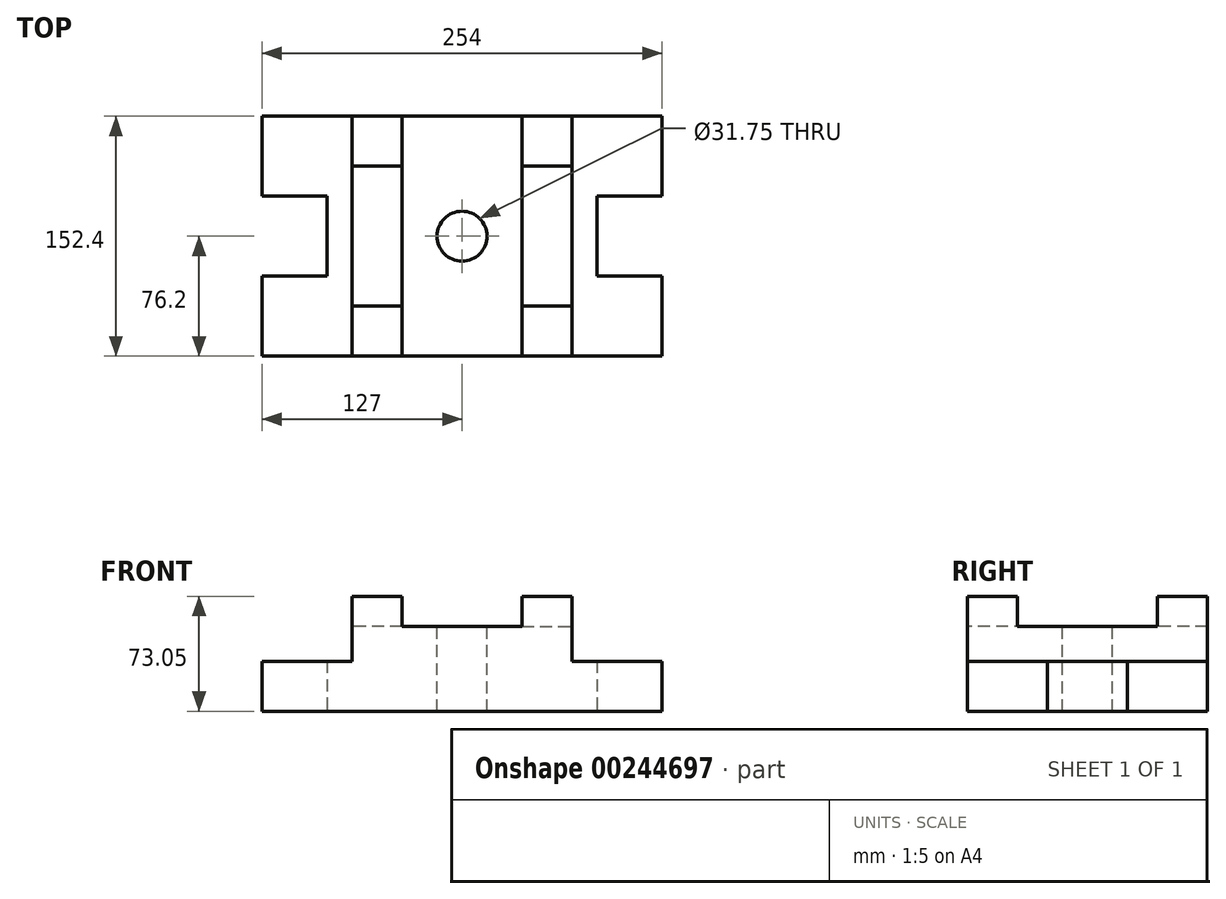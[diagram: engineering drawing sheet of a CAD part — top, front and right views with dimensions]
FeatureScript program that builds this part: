
annotation { "Feature Type Name" : "Feature", "Feature Type Description" : "" }
export const myFeature = defineFeature(function(context is Context, id is Id, definition is map)
    precondition{}
    {
        {
            var Q0;
            Q0=qCreatedBy(makeId("Top.planeOp"),FACE);
            var sketch = newSketch(context, id + "F0", { "sketchPlane" : qUnion([Q0])});
            skLineSegment(sketch, "E0.bottom", {"start": v(127, 76.2) * mm, "end": v(-127, 76.2) * mm});
            skLineSegment(sketch, "E0.top", {"start": v(127, -76.2) * mm, "end": v(-127, -76.2) * mm});
            skPoint(sketch, "E0.middle", {"position": v(0, 0) * mm});
            skLineSegment(sketch, "E1", {"start": v(-127, -76.2) * mm, "end": v(-127, -25.4) * mm});
            skLineSegment(sketch, "E2.bottom", {"start": v(-127, -25.4) * mm, "end": v(-85.72, -25.4) * mm});
            skLineSegment(sketch, "E2.top", {"start": v(-127, 25.4) * mm, "end": v(-85.72, 25.4) * mm});
            skLineSegment(sketch, "E2.right", {"start": v(-85.72, -25.4) * mm, "end": v(-85.72, 25.4) * mm});
            skLineSegment(sketch, "E3", {"start": v(-127, 25.4) * mm, "end": v(-127, 76.2) * mm});
            skLineSegment(sketch, "E4", {"start": v(127, -76.2) * mm, "end": v(127, -25.4) * mm});
            skLineSegment(sketch, "E5.bottom", {"start": v(127, -25.4) * mm, "end": v(85.73, -25.4) * mm});
            skLineSegment(sketch, "E5.top", {"start": v(127, 25.4) * mm, "end": v(85.73, 25.4) * mm});
            skLineSegment(sketch, "E5.right", {"start": v(85.73, -25.4) * mm, "end": v(85.73, 25.4) * mm});
            skLineSegment(sketch, "E6", {"start": v(127, 76.2) * mm, "end": v(127, 25.4) * mm});
            skSolve(sketch);
        }
        {
            var Q0;
            Q0=makeQuery(id+"F0.imprint","IMPRINT",FACE,{"disambiguationData":[TD([[makeQuery(id+"F0.imprint","IMPRINT",EDGE,{"derivedFrom":sQuery(id+"F0.wireOp",EDGE,"E0.bottom")}),1.0]])]});
            extrude(context, id + "F1", {"entities" : qUnion([Q0]), "depth" : 31.75 * mm});
        }
        {
            var Q0;
            Q0=makeQuery(id+"F1.opExtrude","CAP_FACE",FACE,{"disambiguationData":[OSD([sQuery(id+"F0.wireOp",EDGE,"E0.bottom"),sQuery(id+"F0.wireOp",EDGE,"E0.top"),sQuery(id+"F0.wireOp",EDGE,"E1"),sQuery(id+"F0.wireOp",EDGE,"E2.bottom"),sQuery(id+"F0.wireOp",EDGE,"E2.top"),sQuery(id+"F0.wireOp",EDGE,"E2.right"),sQuery(id+"F0.wireOp",EDGE,"E3"),sQuery(id+"F0.wireOp",EDGE,"E4"),sQuery(id+"F0.wireOp",EDGE,"E5.bottom"),sQuery(id+"F0.wireOp",EDGE,"E5.top"),sQuery(id+"F0.wireOp",EDGE,"E5.right"),sQuery(id+"F0.wireOp",EDGE,"E6")])],"isStart":false});
            var sketch = newSketch(context, id + "F2", { "sketchPlane" : qUnion([Q0])});
            skLineSegment(sketch, "E7.bottom", {"start": v(69.85, 76.2) * mm, "end": v(-69.85, 76.2) * mm});
            skLineSegment(sketch, "E7.top", {"start": v(69.85, -76.2) * mm, "end": v(-69.85, -76.2) * mm});
            skLineSegment(sketch, "E7.left", {"start": v(69.85, 76.2) * mm, "end": v(69.85, -76.2) * mm});
            skLineSegment(sketch, "E7.right", {"start": v(-69.85, 76.2) * mm, "end": v(-69.85, -76.2) * mm});
            skPoint(sketch, "E7.middle", {"position": v(0, 0) * mm});
            skSolve(sketch);
        }
        {
            var Q0;
            Q0=makeQuery(id+"F2.imprint","IMPRINT",FACE,{"disambiguationData":[TD([[makeQuery(id+"F2.imprint","IMPRINT",EDGE,{"derivedFrom":sQuery(id+"F2.wireOp",EDGE,"E7.bottom")}),1.0]])]});
            extrude(context, id + "F3", {"entities" : qUnion([Q0]), "operationType" : NewBodyOperationType.ADD, "depth" : 22.22 * mm});
        }
        {
            var Q0;
            Q0=makeQuery(id+"F3.opExtrude","CAP_FACE",FACE,{"disambiguationData":[OSD([sQuery(id+"F2.wireOp",EDGE,"E7.bottom"),sQuery(id+"F2.wireOp",EDGE,"E7.top"),sQuery(id+"F2.wireOp",EDGE,"E7.left"),sQuery(id+"F2.wireOp",EDGE,"E7.right")])],"isStart":false});
            var sketch = newSketch(context, id + "F4", { "sketchPlane" : qUnion([Q0])});
            skCircle(sketch, "E8", {"center": v(0, 0) * mm, "radius": 15.88 * mm});
            skSolve(sketch);
        }
        {
            var Q0;
            Q0=makeQuery(id+"F4.imprint","IMPRINT",FACE,{"disambiguationData":[TD([[makeQuery(id+"F4.imprint","IMPRINT",EDGE,{"derivedFrom":sQuery(id+"F4.wireOp",EDGE,"E8")}),1.0]])]});
            extrude(context, id + "F5", {"entities" : qUnion([Q0]), "operationType" : NewBodyOperationType.REMOVE, "endBound" : BoundingType.THROUGH_ALL, "oppositeDirection" : true, "depth" : 25.4 * mm});
        }
        {
            var Q0;
            Q0=makeQuery(id+"F3.opExtrude","CAP_FACE",FACE,{"disambiguationData":[OSD([sQuery(id+"F2.wireOp",EDGE,"E7.bottom"),sQuery(id+"F2.wireOp",EDGE,"E7.top"),sQuery(id+"F2.wireOp",EDGE,"E7.left"),sQuery(id+"F2.wireOp",EDGE,"E7.right")])],"isStart":false});
            var sketch = newSketch(context, id + "F6", { "sketchPlane" : qUnion([Q0])});
            skLineSegment(sketch, "E9.bottom", {"start": v(-69.85, 76.2) * mm, "end": v(-38.1, 76.2) * mm});
            skLineSegment(sketch, "E9.top", {"start": v(-69.85, -76.2) * mm, "end": v(-38.1, -76.2) * mm});
            skLineSegment(sketch, "E9.left", {"start": v(-69.85, 76.2) * mm, "end": v(-69.85, -76.2) * mm});
            skLineSegment(sketch, "E9.right", {"start": v(-38.1, 76.2) * mm, "end": v(-38.1, -76.2) * mm});
            skLineSegment(sketch, "E10.bottom", {"start": v(69.85, 76.2) * mm, "end": v(38.1, 76.2) * mm});
            skLineSegment(sketch, "E10.top", {"start": v(69.85, -76.2) * mm, "end": v(38.1, -76.2) * mm});
            skLineSegment(sketch, "E10.left", {"start": v(69.85, 76.2) * mm, "end": v(69.85, -76.2) * mm});
            skLineSegment(sketch, "E10.right", {"start": v(38.1, 76.2) * mm, "end": v(38.1, -76.2) * mm});
            skSolve(sketch);
        }
        {
            var Q0;
            Q0=makeQuery(id+"F6.imprint","IMPRINT",FACE,{"disambiguationData":[TD([[makeQuery(id+"F6.imprint","IMPRINT",EDGE,{"derivedFrom":sQuery(id+"F6.wireOp",EDGE,"E10.bottom")}),1.0]])]});
            var Q1;
            Q1=makeQuery(id+"F6.imprint","IMPRINT",FACE,{"disambiguationData":[TD([[makeQuery(id+"F6.imprint","IMPRINT",EDGE,{"derivedFrom":sQuery(id+"F6.wireOp",EDGE,"E9.bottom")}),1.0]])]});
            extrude(context, id + "F7", {"entities" : qUnion([Q0, Q1]), "operationType" : NewBodyOperationType.ADD, "depth" : 3 / 101.6 * mm});
        }
        {
            var Q0;
            Q0=makeQuery(id+"F7.opExtrude","CAP_FACE",FACE,{"disambiguationData":[OSD([sQuery(id+"F6.wireOp",EDGE,"E10.bottom"),sQuery(id+"F6.wireOp",EDGE,"E10.top"),sQuery(id+"F6.wireOp",EDGE,"E10.left"),sQuery(id+"F6.wireOp",EDGE,"E10.right")])],"isStart":false});
            var sketch = newSketch(context, id + "F8", { "sketchPlane" : qUnion([Q0])});
            skLineSegment(sketch, "E11.bottom", {"start": v(38.1, 76.2) * mm, "end": v(69.85, 76.2) * mm});
            skLineSegment(sketch, "E11.top", {"start": v(38.1, 44.45) * mm, "end": v(69.85, 44.45) * mm});
            skLineSegment(sketch, "E11.left", {"start": v(38.1, 76.2) * mm, "end": v(38.1, 44.45) * mm});
            skLineSegment(sketch, "E11.right", {"start": v(69.85, 76.2) * mm, "end": v(69.85, 44.45) * mm});
            skLineSegment(sketch, "E12.bottom", {"start": v(38.1, -44.45) * mm, "end": v(69.85, -44.45) * mm});
            skLineSegment(sketch, "E12.top", {"start": v(38.1, -76.2) * mm, "end": v(69.85, -76.2) * mm});
            skLineSegment(sketch, "E12.left", {"start": v(38.1, -44.45) * mm, "end": v(38.1, -76.2) * mm});
            skLineSegment(sketch, "E12.right", {"start": v(69.85, -44.45) * mm, "end": v(69.85, -76.2) * mm});
            skSolve(sketch);
        }
        {
            var Q0;
            Q0=makeQuery(id+"F7.opExtrude","CAP_FACE",FACE,{"disambiguationData":[OSD([sQuery(id+"F6.wireOp",EDGE,"E9.bottom"),sQuery(id+"F6.wireOp",EDGE,"E9.top"),sQuery(id+"F6.wireOp",EDGE,"E9.left"),sQuery(id+"F6.wireOp",EDGE,"E9.right")])],"isStart":false});
            var sketch = newSketch(context, id + "F9", { "sketchPlane" : qUnion([Q0])});
            skLineSegment(sketch, "E13.bottom", {"start": v(-69.85, -76.2) * mm, "end": v(-38.1, -76.2) * mm});
            skLineSegment(sketch, "E13.top", {"start": v(-69.85, -44.45) * mm, "end": v(-38.1, -44.45) * mm});
            skLineSegment(sketch, "E13.left", {"start": v(-69.85, -76.2) * mm, "end": v(-69.85, -44.45) * mm});
            skLineSegment(sketch, "E13.right", {"start": v(-38.1, -76.2) * mm, "end": v(-38.1, -44.45) * mm});
            skLineSegment(sketch, "E14.bottom", {"start": v(-38.1, 76.2) * mm, "end": v(-69.85, 76.2) * mm});
            skLineSegment(sketch, "E14.top", {"start": v(-38.1, 44.45) * mm, "end": v(-69.85, 44.45) * mm});
            skLineSegment(sketch, "E14.left", {"start": v(-38.1, 76.2) * mm, "end": v(-38.1, 44.45) * mm});
            skLineSegment(sketch, "E14.right", {"start": v(-69.85, 76.2) * mm, "end": v(-69.85, 44.45) * mm});
            skSolve(sketch);
        }
        {
            var Q0;
            Q0=makeQuery(id+"F9.imprint","IMPRINT",FACE,{"disambiguationData":[TD([[makeQuery(id+"F9.imprint","IMPRINT",EDGE,{"derivedFrom":sQuery(id+"F9.wireOp",EDGE,"E13.bottom")}),-1.0]])]});
            var Q1;
            Q1=makeQuery(id+"F9.imprint","IMPRINT",FACE,{"disambiguationData":[TD([[makeQuery(id+"F9.imprint","IMPRINT",EDGE,{"derivedFrom":sQuery(id+"F9.wireOp",EDGE,"E14.bottom")}),1.0]])]});
            var Q2;
            Q2=makeQuery(id+"F8.imprint","IMPRINT",FACE,{"disambiguationData":[TD([[makeQuery(id+"F8.imprint","IMPRINT",EDGE,{"derivedFrom":sQuery(id+"F8.wireOp",EDGE,"E11.bottom")}),1.0]])]});
            var Q3;
            Q3=makeQuery(id+"F8.imprint","IMPRINT",FACE,{"disambiguationData":[TD([[makeQuery(id+"F8.imprint","IMPRINT",EDGE,{"derivedFrom":sQuery(id+"F8.wireOp",EDGE,"E12.bottom")}),-1.0]])]});
            extrude(context, id + "F10", {"entities" : qUnion([Q0, Q1, Q2, Q3]), "operationType" : NewBodyOperationType.ADD, "depth" : 19.05 * mm});
        }
    });
